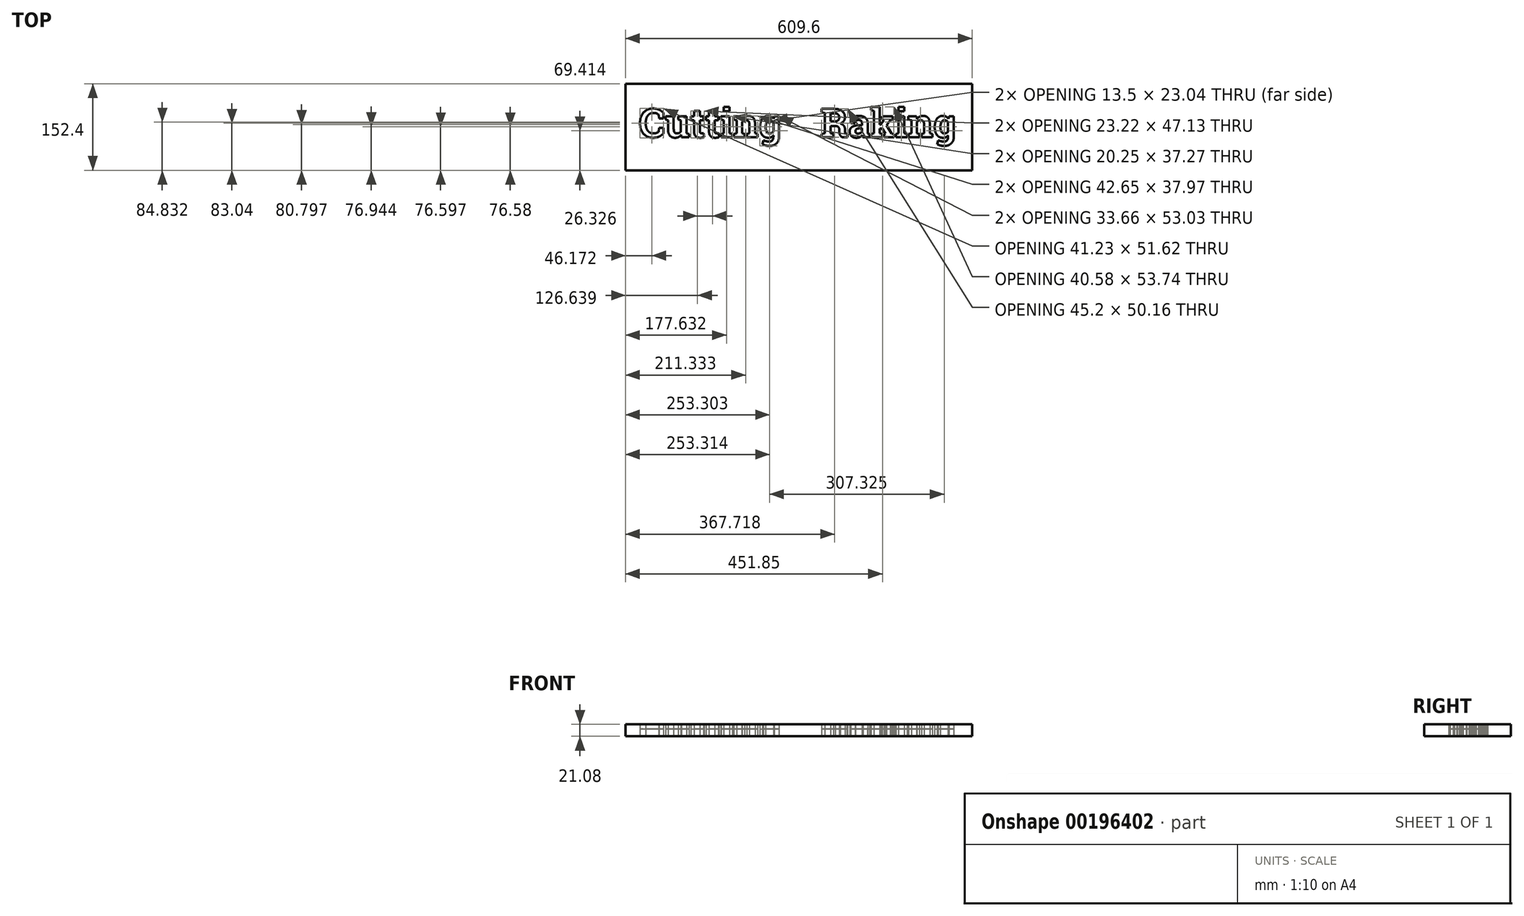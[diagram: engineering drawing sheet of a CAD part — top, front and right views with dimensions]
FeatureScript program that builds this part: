
annotation { "Feature Type Name" : "Feature", "Feature Type Description" : "" }
export const myFeature = defineFeature(function(context is Context, id is Id, definition is map)
    precondition{}
    {
        {
            var Q0;
            Q0=qCreatedBy(makeId("Top.planeOp"),FACE);
            var sketch = newSketch(context, id + "F0", { "sketchPlane" : qUnion([Q0])});
            skLineSegment(sketch, "E0.bottom", {"start": v(-298.76, 43.64) * mm, "end": v(310.84, 43.64) * mm});
            skLineSegment(sketch, "E0.top", {"start": v(-298.76, -108.76) * mm, "end": v(310.84, -108.76) * mm});
            skLineSegment(sketch, "E0.left", {"start": v(-298.76, 43.64) * mm, "end": v(-298.76, -108.76) * mm});
            skLineSegment(sketch, "E0.right", {"start": v(310.84, 43.64) * mm, "end": v(310.84, -108.76) * mm});
            skText(sketch, "E1", { "text": "Cutting    Raking\n", "fontName": "RobotoSlab-Bold.ttf"});
            const initialGuessF0  = {"E1": [-0.275, -0.0508, 1, 0, 0.0508]};
            skSetInitialGuess(sketch, initialGuessF0);
            skSolve(sketch);
        }
        {
            var Q0;
            Q0=makeQuery(id+"F0.imprint","IMPRINT",FACE,{"disambiguationData":[TD([[makeQuery(id+"F0.imprint","IMPRINT",EDGE,{"derivedFrom":sQuery(id+"F0.wireOp",EDGE,"E0.bottom")}),-1.0]])]});
            var Q1;
            Q1=makeQuery(id+"F0.imprint","IMPRINT",FACE,{"disambiguationData":[TD([[makeQuery(id+"F0.imprint","IMPRINT",EDGE,{"derivedFrom":sQuery(id+"F0.wireOp",EDGE,"E1.sketch_text.stroke-150")}),1.0]])]});
            var Q2;
            Q2=makeQuery(id+"F0.imprint","IMPRINT",FACE,{"disambiguationData":[TD([[makeQuery(id+"F0.imprint","IMPRINT",EDGE,{"derivedFrom":sQuery(id+"F0.wireOp",EDGE,"E1.sketch_text.stroke-189")}),1.0]])]});
            var Q3;
            Q3=makeQuery(id+"F0.imprint","IMPRINT",FACE,{"disambiguationData":[TD([[makeQuery(id+"F0.imprint","IMPRINT",EDGE,{"derivedFrom":sQuery(id+"F0.wireOp",EDGE,"E1.sketch_text.stroke-320")}),1.0]])]});
            var Q4;
            Q4=makeQuery(id+"F0.imprint","IMPRINT",FACE,{"disambiguationData":[TD([[makeQuery(id+"F0.imprint","IMPRINT",EDGE,{"derivedFrom":sQuery(id+"F0.wireOp",EDGE,"E1.sketch_text.stroke-223")}),1.0]])]});
            extrude(context, id + "F1", {"entities" : qUnion([Q0, Q1, Q2, Q3, Q4]), "depth" : 21.08 * mm});
        }
        {
            var Q0;
            Q0=makeQuery(id+"F0.imprint","IMPRINT",FACE,{"disambiguationData":[TD([[makeQuery(id+"F0.imprint","IMPRINT",EDGE,{"derivedFrom":sQuery(id+"F0.wireOp",EDGE,"E1.sketch_text.stroke-0")}),-1.0]])]});
            var Q1;
            Q1=makeQuery(id+"F0.imprint","IMPRINT",FACE,{"disambiguationData":[TD([[makeQuery(id+"F0.imprint","IMPRINT",EDGE,{"derivedFrom":sQuery(id+"F0.wireOp",EDGE,"E1.sketch_text.stroke-24")}),-1.0]])]});
            var Q2;
            Q2=makeQuery(id+"F0.imprint","IMPRINT",FACE,{"disambiguationData":[TD([[makeQuery(id+"F0.imprint","IMPRINT",EDGE,{"derivedFrom":sQuery(id+"F0.wireOp",EDGE,"E1.sketch_text.stroke-48")}),-1.0]])]});
            var Q3;
            Q3=makeQuery(id+"F0.imprint","IMPRINT",FACE,{"disambiguationData":[TD([[makeQuery(id+"F0.imprint","IMPRINT",EDGE,{"derivedFrom":sQuery(id+"F0.wireOp",EDGE,"E1.sketch_text.stroke-68")}),-1.0]])]});
            var Q4;
            Q4=makeQuery(id+"F0.imprint","IMPRINT",FACE,{"disambiguationData":[TD([[makeQuery(id+"F0.imprint","IMPRINT",EDGE,{"derivedFrom":sQuery(id+"F0.wireOp",EDGE,"E1.sketch_text.stroke-88")}),-1.0]])]});
            var Q5;
            Q5=makeQuery(id+"F0.imprint","IMPRINT",FACE,{"disambiguationData":[TD([[makeQuery(id+"F0.imprint","IMPRINT",EDGE,{"derivedFrom":sQuery(id+"F0.wireOp",EDGE,"E1.sketch_text.stroke-102")}),-1.0]])]});
            var Q6;
            Q6=makeQuery(id+"F0.imprint","IMPRINT",FACE,{"disambiguationData":[TD([[makeQuery(id+"F0.imprint","IMPRINT",EDGE,{"derivedFrom":sQuery(id+"F0.wireOp",EDGE,"E1.sketch_text.stroke-98")}),-1.0]])]});
            var Q7;
            Q7=makeQuery(id+"F0.imprint","IMPRINT",FACE,{"disambiguationData":[TD([[makeQuery(id+"F0.imprint","IMPRINT",EDGE,{"derivedFrom":sQuery(id+"F0.wireOp",EDGE,"E1.sketch_text.stroke-128")}),-1.0]])]});
            var Q8;
            Q8=makeQuery(id+"F0.imprint","IMPRINT",FACE,{"disambiguationData":[TD([[makeQuery(id+"F0.imprint","IMPRINT",EDGE,{"derivedFrom":sQuery(id+"F0.wireOp",EDGE,"E1.sketch_text.stroke-160")}),-1.0]])]});
            var Q9;
            Q9=makeQuery(id+"F0.imprint","IMPRINT",FACE,{"disambiguationData":[TD([[makeQuery(id+"F0.imprint","IMPRINT",EDGE,{"derivedFrom":sQuery(id+"F0.wireOp",EDGE,"E1.sketch_text.stroke-196")}),-1.0]])]});
            var Q10;
            Q10=makeQuery(id+"F0.imprint","IMPRINT",FACE,{"disambiguationData":[TD([[makeQuery(id+"F0.imprint","IMPRINT",EDGE,{"derivedFrom":sQuery(id+"F0.wireOp",EDGE,"E1.sketch_text.stroke-231")}),-1.0]])]});
            var Q11;
            Q11=makeQuery(id+"F0.imprint","IMPRINT",FACE,{"disambiguationData":[TD([[makeQuery(id+"F0.imprint","IMPRINT",EDGE,{"derivedFrom":sQuery(id+"F0.wireOp",EDGE,"E1.sketch_text.stroke-258")}),-1.0]])]});
            var Q12;
            Q12=makeQuery(id+"F0.imprint","IMPRINT",FACE,{"disambiguationData":[TD([[makeQuery(id+"F0.imprint","IMPRINT",EDGE,{"derivedFrom":sQuery(id+"F0.wireOp",EDGE,"E1.sketch_text.stroke-272")}),-1.0]])]});
            var Q13;
            Q13=makeQuery(id+"F0.imprint","IMPRINT",FACE,{"disambiguationData":[TD([[makeQuery(id+"F0.imprint","IMPRINT",EDGE,{"derivedFrom":sQuery(id+"F0.wireOp",EDGE,"E1.sketch_text.stroke-298")}),-1.0]])]});
            var Q14;
            Q14=makeQuery(id+"F0.imprint","IMPRINT",FACE,{"disambiguationData":[TD([[makeQuery(id+"F0.imprint","IMPRINT",EDGE,{"derivedFrom":sQuery(id+"F0.wireOp",EDGE,"E1.sketch_text.stroke-268")}),-1.0]])]});
            extrude(context, id + "F2", {"entities" : qUnion([Q0, Q1, Q2, Q3, Q4, Q5, Q6, Q7, Q8, Q9, Q10, Q11, Q12, Q13, Q14]), "depth" : 12.7 * mm});
        }
    });
